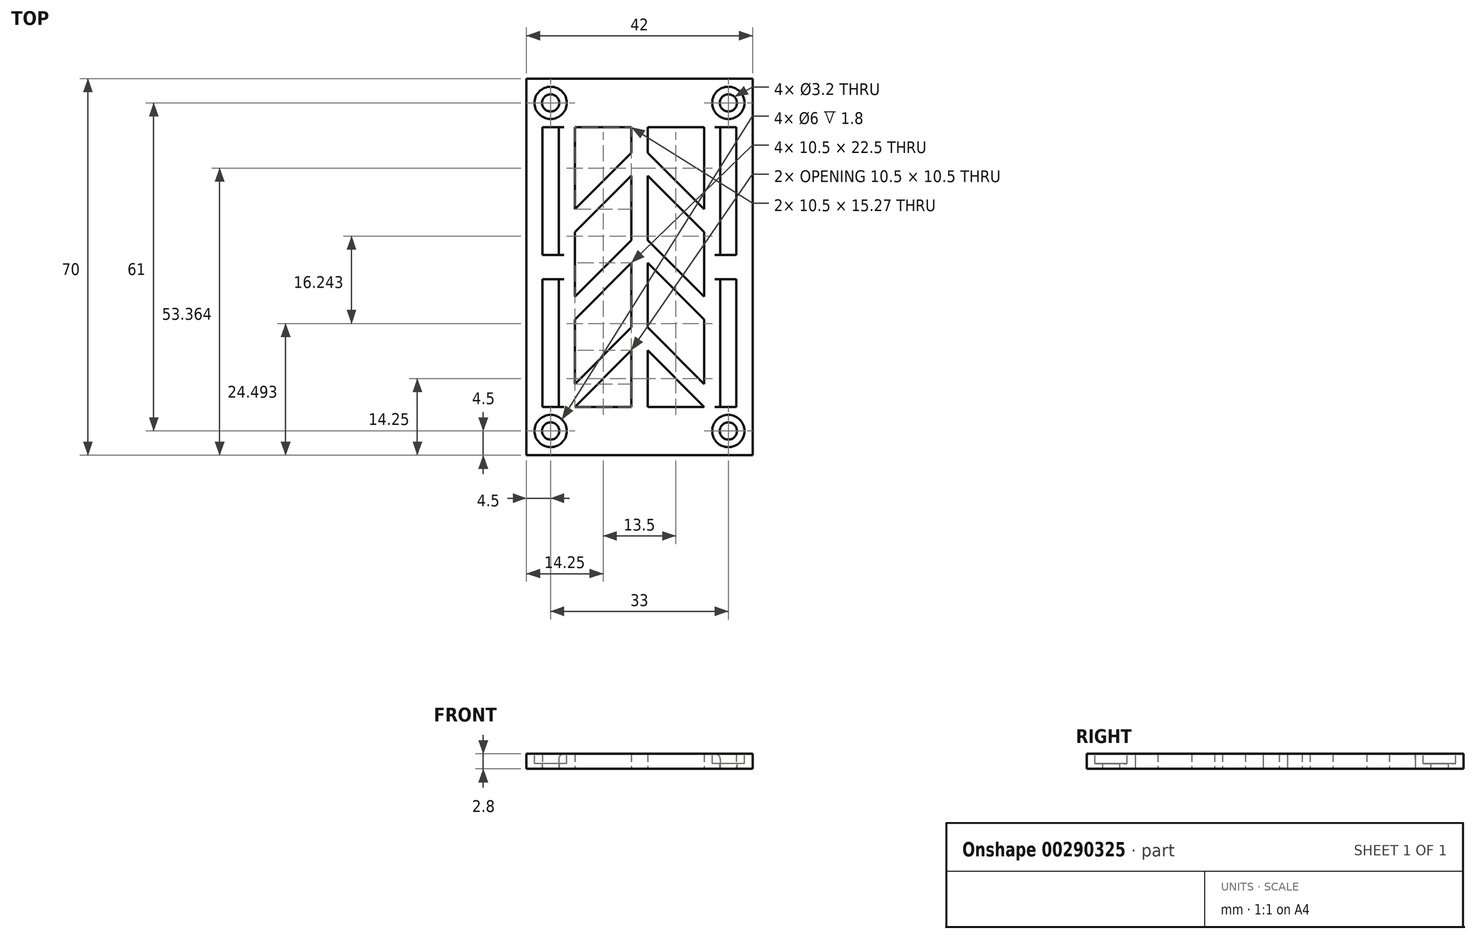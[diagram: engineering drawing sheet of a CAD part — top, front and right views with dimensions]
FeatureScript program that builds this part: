
annotation { "Feature Type Name" : "Feature", "Feature Type Description" : "" }
export const myFeature = defineFeature(function(context is Context, id is Id, definition is map)
    precondition{}
    {
        {
            var Q0;
            Q0=qCreatedBy(makeId("Top.planeOp"),FACE);
            var sketch = newSketch(context, id + "F0", { "sketchPlane" : qUnion([Q0])});
            skLineSegment(sketch, "E0.bottom", {"start": v(-21, 35) * mm, "end": v(21, 35) * mm});
            skLineSegment(sketch, "E0.top", {"start": v(-21, -35) * mm, "end": v(21, -35) * mm});
            skLineSegment(sketch, "E0.left", {"start": v(-21, 35) * mm, "end": v(-21, -35) * mm});
            skLineSegment(sketch, "E0.right", {"start": v(21, 35) * mm, "end": v(21, -35) * mm});
            skPoint(sketch, "E0.middle", {"position": v(0, 0) * mm});
            skLineSegment(sketch, "E1", {"start": v(21, -35) * mm, "end": v(16.5, -35) * mm, "construction": true});
            skLineSegment(sketch, "E2", {"start": v(21, -35) * mm, "end": v(21, -30.5) * mm, "construction": true});
            skCircle(sketch, "E3", {"center": v(16.5, -30.5) * mm, "radius": 1.6 * mm});
            skLineSegment(sketch, "E4", {"start": v(-21, -35) * mm, "end": v(-16.5, -35) * mm, "construction": true});
            skCircle(sketch, "E5", {"center": v(-16.5, -30.5) * mm, "radius": 1.6 * mm});
            skLineSegment(sketch, "E6", {"start": v(-21, 35) * mm, "end": v(-21, 30.5) * mm, "construction": true});
            skCircle(sketch, "E7", {"center": v(-16.5, 30.5) * mm, "radius": 1.6 * mm});
            skCircle(sketch, "E8", {"center": v(16.5, 30.5) * mm, "radius": 1.6 * mm});
            skSolve(sketch);
        }
        {
            var Q0;
            Q0=makeQuery(id+"F0.imprint","IMPRINT",FACE,{"disambiguationData":[TD([[makeQuery(id+"F0.imprint","IMPRINT",EDGE,{"derivedFrom":sQuery(id+"F0.wireOp",EDGE,"E0.bottom")}),-1.0]])]});
            var sketch = newSketch(context, id + "F1", { "sketchPlane" : qUnion([Q0])});
            skPoint(sketch, "E9.0", {"position": v(-16.5, 30.5) * mm});
            skCircle(sketch, "E9.1", {"center": v(-16.5, 30.5) * mm, "radius": 1.6 * mm});
            skCircle(sketch, "E10.0", {"center": v(16.5, 30.5) * mm, "radius": 1.6 * mm});
            skPoint(sketch, "E10.1", {"position": v(16.5, 30.5) * mm});
            skCircle(sketch, "E11.0", {"center": v(-16.5, -30.5) * mm, "radius": 1.6 * mm});
            skPoint(sketch, "E11.1", {"position": v(-16.5, -30.5) * mm});
            skPoint(sketch, "E11.2", {"position": v(16.5, -30.5) * mm});
            skCircle(sketch, "E11.3", {"center": v(16.5, -30.5) * mm, "radius": 1.6 * mm});
            skCircle(sketch, "E12", {"center": v(-16.5, -30.5) * mm, "radius": 3 * mm, "construction": true});
            skCircle(sketch, "E13", {"center": v(16.5, -30.5) * mm, "radius": 3 * mm, "construction": true});
            skCircle(sketch, "E14", {"center": v(16.5, 30.5) * mm, "radius": 3 * mm, "construction": true});
            skCircle(sketch, "E15", {"center": v(-16.5, 30.5) * mm, "radius": 3 * mm, "construction": true});
            skPoint(sketch, "E16.endSnap0", {"position": v(-21, 0) * mm});
            skLineSegment(sketch, "E17.0", {"start": v(-21, 35) * mm, "end": v(-21, -35) * mm});
            skLineSegment(sketch, "E18.0", {"start": v(21, 35) * mm, "end": v(21, -35) * mm});
            skLineSegment(sketch, "E18.1", {"start": v(-21, -35) * mm, "end": v(21, -35) * mm});
            skLineSegment(sketch, "E18.2", {"start": v(-21, 35) * mm, "end": v(21, 35) * mm});
            skLineSegment(sketch, "E19", {"start": v(-12, 26) * mm, "end": v(-12, 10.73) * mm});
            skLineSegment(sketch, "E20", {"start": v(18, 26) * mm, "end": v(18, 2.25) * mm});
            skLineSegment(sketch, "E21", {"start": v(12, 26) * mm, "end": v(12, 10.73) * mm});
            skLineSegment(sketch, "E22", {"start": v(-18, -26) * mm, "end": v(-15, -26) * mm});
            skLineSegment(sketch, "E23.trimOffspring", {"start": v(-18, 26) * mm, "end": v(-18, 2.25) * mm});
            skLineSegment(sketch, "E24.trimOffspring", {"start": v(-15, 26) * mm, "end": v(-15, 2.25) * mm});
            skLineSegment(sketch, "E25.trimOffspring", {"start": v(15, 26) * mm, "end": v(15, 2.25) * mm});
            skLineSegment(sketch, "E26", {"start": v(-1.5, -15.5) * mm, "end": v(-12, -26) * mm});
            skLineSegment(sketch, "E27", {"start": v(1.5, -15.5) * mm, "end": v(12, -26) * mm});
            skLineSegment(sketch, "E28", {"start": v(-1.5, -11.26) * mm, "end": v(-12, -21.76) * mm});
            skLineSegment(sketch, "E29", {"start": v(1.5, -11.26) * mm, "end": v(12, -21.76) * mm});
            skLineSegment(sketch, "E30", {"start": v(-1.5, 0.74) * mm, "end": v(-12, -9.76) * mm});
            skLineSegment(sketch, "E31", {"start": v(1.5, 0.74) * mm, "end": v(12, -9.76) * mm});
            skLineSegment(sketch, "E32", {"start": v(-1.5, 4.99) * mm, "end": v(-12, -5.51) * mm});
            skLineSegment(sketch, "E33", {"start": v(1.5, 4.99) * mm, "end": v(12, -5.51) * mm});
            skLineSegment(sketch, "E34", {"start": v(-1.5, 16.99) * mm, "end": v(-12, 6.49) * mm});
            skLineSegment(sketch, "E35", {"start": v(1.5, 16.99) * mm, "end": v(12, 6.49) * mm});
            skLineSegment(sketch, "E36", {"start": v(-1.5, 21.23) * mm, "end": v(-12, 10.73) * mm});
            skLineSegment(sketch, "E37", {"start": v(1.5, 21.23) * mm, "end": v(12, 10.73) * mm});
            skLineSegment(sketch, "E38", {"start": v(-1.5, 26) * mm, "end": v(-1.5, 21.23) * mm});
            skLineSegment(sketch, "E39", {"start": v(1.5, 26) * mm, "end": v(1.5, 21.23) * mm});
            skLineSegment(sketch, "E40", {"start": v(-18, 26) * mm, "end": v(-15, 26) * mm});
            skLineSegment(sketch, "E41.trimOffspring", {"start": v(-12, 6.49) * mm, "end": v(-12, -5.51) * mm});
            skLineSegment(sketch, "E42.trimOffspring", {"start": v(-12, -9.76) * mm, "end": v(-12, -21.76) * mm});
            skLineSegment(sketch, "E43.trimOffspring", {"start": v(12, -9.76) * mm, "end": v(12, -21.76) * mm});
            skLineSegment(sketch, "E44.trimOffspring", {"start": v(-1.5, -15.5) * mm, "end": v(-1.5, -26) * mm});
            skLineSegment(sketch, "E45.trimOffspring", {"start": v(1.5, -15.5) * mm, "end": v(1.5, -26) * mm});
            skPoint(sketch, "E46.start.orphan", {"position": v(0, -26) * mm});
            skLineSegment(sketch, "E47.trimOffspring", {"start": v(-1.5, 0.74) * mm, "end": v(-1.5, -11.26) * mm});
            skLineSegment(sketch, "E48.trimOffspring", {"start": v(1.5, 0.74) * mm, "end": v(1.5, -11.26) * mm});
            skLineSegment(sketch, "E49.trimOffspring", {"start": v(1.5, -26) * mm, "end": v(12, -26) * mm});
            skLineSegment(sketch, "E50.trimOffspring", {"start": v(15, -26) * mm, "end": v(18, -26) * mm});
            skLineSegment(sketch, "E51.trimOffspring", {"start": v(-12, -26) * mm, "end": v(-1.5, -26) * mm});
            skPoint(sketch, "E52.orphan", {"position": v(-21, -26) * mm});
            skLineSegment(sketch, "E53.trimOffspring", {"start": v(-1.5, 16.99) * mm, "end": v(-1.5, 4.99) * mm});
            skLineSegment(sketch, "E54.trimOffspring", {"start": v(1.5, 26) * mm, "end": v(12, 26) * mm});
            skLineSegment(sketch, "E55.trimOffspring", {"start": v(1.5, 16.99) * mm, "end": v(1.5, 4.99) * mm});
            skLineSegment(sketch, "E56.trimOffspring", {"start": v(12, 6.49) * mm, "end": v(12, -5.51) * mm});
            skLineSegment(sketch, "E57.trimOffspring", {"start": v(-12, 26) * mm, "end": v(-1.5, 26) * mm});
            skLineSegment(sketch, "E58.trimOffspring", {"start": v(15, 26) * mm, "end": v(18, 26) * mm});
            skPoint(sketch, "E59.orphan", {"position": v(-21, 26) * mm});
            skPoint(sketch, "E60.orphan", {"position": v(21, 26) * mm});
            skPoint(sketch, "E61.orphan", {"position": v(21, -26) * mm});
            skLineSegment(sketch, "E62.trimOffspring", {"start": v(-15, 2.25) * mm, "end": v(-18, 2.25) * mm});
            skPoint(sketch, "E63.trimOffspring.end.orphan", {"position": v(21, 0) * mm});
            skLineSegment(sketch, "E64.trimOffspring", {"start": v(-15, -2.25) * mm, "end": v(-18, -2.25) * mm});
            skLineSegment(sketch, "E65.trimOffspring", {"start": v(15, -2.25) * mm, "end": v(18, -2.25) * mm});
            skLineSegment(sketch, "E66.trimOffspring", {"start": v(15, 2.25) * mm, "end": v(18, 2.25) * mm});
            skLineSegment(sketch, "E67.trimOffspring", {"start": v(-18, -2.25) * mm, "end": v(-18, -26) * mm});
            skLineSegment(sketch, "E68.trimOffspring", {"start": v(-15, -2.25) * mm, "end": v(-15, -26) * mm});
            skLineSegment(sketch, "E69.trimOffspring", {"start": v(15, -2.25) * mm, "end": v(15, -26) * mm});
            skLineSegment(sketch, "E70.trimOffspring", {"start": v(18, -2.25) * mm, "end": v(18, -26) * mm});
            skSolve(sketch);
        }
        {
            var Q0;
            Q0 = qSketchRegion(id + "F1", true);
            extrude(context, id + "F2", {"entities" : qUnion([Q0]), "depth" : 2.8 * mm});
        }
        {
            var Q0;
            Q0=makeQuery(id+"F2.opExtrude","CAP_FACE",FACE,{"disambiguationData":[OSD([sQuery(id+"F1.wireOp",EDGE,"E9.1"),sQuery(id+"F1.wireOp",EDGE,"E10.0"),sQuery(id+"F1.wireOp",EDGE,"E11.0"),sQuery(id+"F1.wireOp",EDGE,"E11.3"),sQuery(id+"F1.wireOp",EDGE,"E17.0"),sQuery(id+"F1.wireOp",EDGE,"E18.0"),sQuery(id+"F1.wireOp",EDGE,"E18.1"),sQuery(id+"F1.wireOp",EDGE,"E18.2"),sQuery(id+"F1.wireOp",EDGE,"E19"),sQuery(id+"F1.wireOp",EDGE,"E20"),sQuery(id+"F1.wireOp",EDGE,"E21"),sQuery(id+"F1.wireOp",EDGE,"E22"),sQuery(id+"F1.wireOp",EDGE,"E23.trimOffspring"),sQuery(id+"F1.wireOp",EDGE,"E24.trimOffspring"),sQuery(id+"F1.wireOp",EDGE,"E25.trimOffspring"),sQuery(id+"F1.wireOp",EDGE,"E26"),sQuery(id+"F1.wireOp",EDGE,"E27"),sQuery(id+"F1.wireOp",EDGE,"E28"),sQuery(id+"F1.wireOp",EDGE,"E29"),sQuery(id+"F1.wireOp",EDGE,"E30"),sQuery(id+"F1.wireOp",EDGE,"E31"),sQuery(id+"F1.wireOp",EDGE,"E32"),sQuery(id+"F1.wireOp",EDGE,"E33"),sQuery(id+"F1.wireOp",EDGE,"E34"),sQuery(id+"F1.wireOp",EDGE,"E35"),sQuery(id+"F1.wireOp",EDGE,"E36"),sQuery(id+"F1.wireOp",EDGE,"E37"),sQuery(id+"F1.wireOp",EDGE,"E38"),sQuery(id+"F1.wireOp",EDGE,"E39"),sQuery(id+"F1.wireOp",EDGE,"E40"),sQuery(id+"F1.wireOp",EDGE,"E41.trimOffspring"),sQuery(id+"F1.wireOp",EDGE,"E42.trimOffspring"),sQuery(id+"F1.wireOp",EDGE,"E43.trimOffspring"),sQuery(id+"F1.wireOp",EDGE,"E44.trimOffspring"),sQuery(id+"F1.wireOp",EDGE,"E45.trimOffspring"),sQuery(id+"F1.wireOp",EDGE,"E47.trimOffspring"),sQuery(id+"F1.wireOp",EDGE,"E48.trimOffspring"),sQuery(id+"F1.wireOp",EDGE,"E49.trimOffspring"),sQuery(id+"F1.wireOp",EDGE,"E50.trimOffspring"),sQuery(id+"F1.wireOp",EDGE,"E51.trimOffspring"),sQuery(id+"F1.wireOp",EDGE,"E53.trimOffspring"),sQuery(id+"F1.wireOp",EDGE,"E54.trimOffspring"),sQuery(id+"F1.wireOp",EDGE,"E55.trimOffspring"),sQuery(id+"F1.wireOp",EDGE,"E56.trimOffspring"),sQuery(id+"F1.wireOp",EDGE,"E57.trimOffspring"),sQuery(id+"F1.wireOp",EDGE,"E58.trimOffspring"),sQuery(id+"F1.wireOp",EDGE,"E62.trimOffspring"),sQuery(id+"F1.wireOp",EDGE,"E64.trimOffspring"),sQuery(id+"F1.wireOp",EDGE,"E65.trimOffspring"),sQuery(id+"F1.wireOp",EDGE,"E66.trimOffspring"),sQuery(id+"F1.wireOp",EDGE,"E67.trimOffspring"),sQuery(id+"F1.wireOp",EDGE,"E68.trimOffspring"),sQuery(id+"F1.wireOp",EDGE,"E69.trimOffspring"),sQuery(id+"F1.wireOp",EDGE,"E70.trimOffspring")])],"isStart":false});
            var sketch = newSketch(context, id + "F3", { "sketchPlane" : qUnion([Q0])});
            skCircle(sketch, "E71.0", {"center": v(-16.5, -30.5) * mm, "radius": 3 * mm});
            skCircle(sketch, "E72.0", {"center": v(16.5, -30.5) * mm, "radius": 3 * mm});
            skCircle(sketch, "E73.0", {"center": v(-16.5, 30.5) * mm, "radius": 3 * mm});
            skCircle(sketch, "E73.1", {"center": v(16.5, 30.5) * mm, "radius": 3 * mm});
            skSolve(sketch);
        }
        {
            var Q0;
            Q0 = qSketchRegion(id + "F3", true);
            extrude(context, id + "F4", {"entities" : qUnion([Q0]), "operationType" : NewBodyOperationType.REMOVE, "oppositeDirection" : true, "depth" : 1.8 * mm});
        }
        {
            var Q0;
            Q0=makeQuery(id+"F2.opExtrude","CAP_EDGE",EDGE,{"disambiguationData":[OSD([sQuery(id+"F1.wireOp",EDGE,"E24.trimOffspring")])],"isStart":false});
            var Q1;
            Q1=makeQuery(id+"F2.opExtrude","CAP_EDGE",EDGE,{"disambiguationData":[OSD([sQuery(id+"F1.wireOp",EDGE,"E25.trimOffspring")])],"isStart":false});
            var Q2;
            Q2=makeQuery(id+"F2.opExtrude","CAP_EDGE",EDGE,{"disambiguationData":[OSD([sQuery(id+"F1.wireOp",EDGE,"E68.trimOffspring")])],"isStart":false});
            var Q3;
            Q3=makeQuery(id+"F2.opExtrude","CAP_EDGE",EDGE,{"disambiguationData":[OSD([sQuery(id+"F1.wireOp",EDGE,"E69.trimOffspring")])],"isStart":false});
            fillet(context, id + "F5", {"entities" : qUnion([Q0, Q1, Q2, Q3]), "radius" : 1 * mm, "tangentPropagation" : true, "allowEdgeOverflow" : false});
        }
    });
